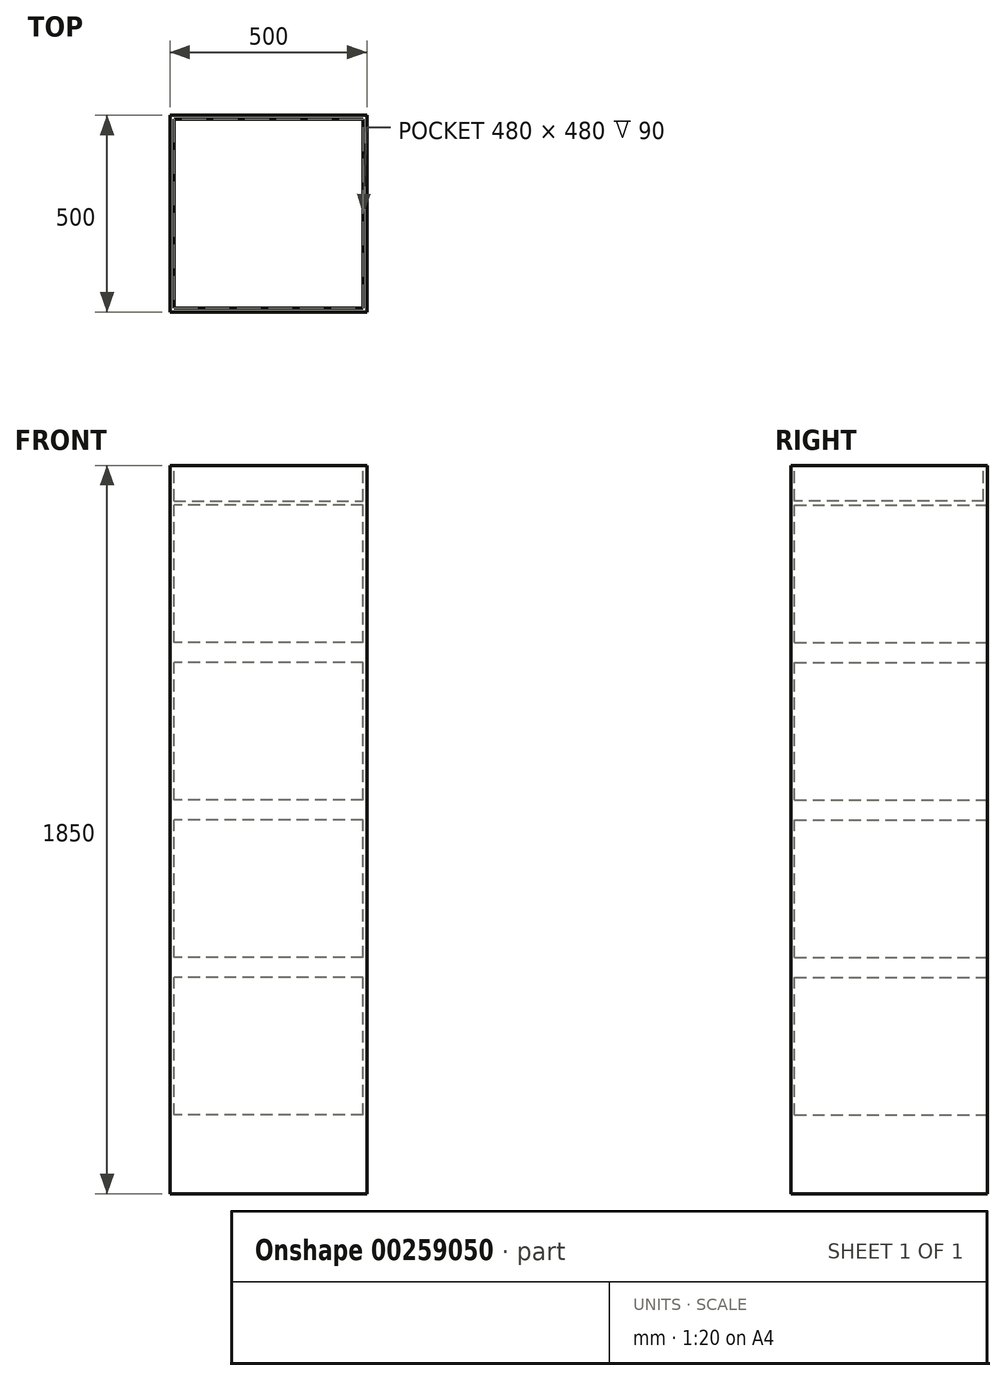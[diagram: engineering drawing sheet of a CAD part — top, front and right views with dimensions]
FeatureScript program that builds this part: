
annotation { "Feature Type Name" : "Feature", "Feature Type Description" : "" }
export const myFeature = defineFeature(function(context is Context, id is Id, definition is map)
    precondition{}
    {
        {
            var Q0;
            Q0=qCreatedBy(makeId("Top.planeOp"),FACE);
            var sketch = newSketch(context, id + "F0", { "sketchPlane" : qUnion([Q0])});
            skLineSegment(sketch, "E0.bottom", {"start": v(0, 0) * mm, "end": v(-500, 0) * mm});
            skLineSegment(sketch, "E0.top", {"start": v(0, 500) * mm, "end": v(-500, 500) * mm});
            skLineSegment(sketch, "E0.left", {"start": v(0, 0) * mm, "end": v(0, 500) * mm});
            skLineSegment(sketch, "E0.right", {"start": v(-500, 0) * mm, "end": v(-500, 500) * mm});
            skSolve(sketch);
        }
        {
            var Q0;
            Q0=makeQuery(id+"F0.imprint","IMPRINT",FACE,{"disambiguationData":[TD([[makeQuery(id+"F0.imprint","IMPRINT",EDGE,{"derivedFrom":sQuery(id+"F0.wireOp",EDGE,"E0.bottom")}),-1.0]])]});
            extrude(context, id + "F1", {"entities" : qUnion([Q0]), "depth" : 1850 * mm});
        }
        {
            var Q0;
            Q0=makeQuery(id+"F1.opExtrude","SWEPT_FACE",FACE,{"disambiguationData":[OSD([sQuery(id+"F0.wireOp",EDGE,"E0.top")])]});
            var sketch = newSketch(context, id + "F2", { "sketchPlane" : qUnion([Q0])});
            skLineSegment(sketch, "E1.bottom", {"start": v(10, 200) * mm, "end": v(490, 200) * mm});
            skLineSegment(sketch, "E1.top", {"start": v(10, 550) * mm, "end": v(490, 550) * mm});
            skLineSegment(sketch, "E1.left", {"start": v(10, 200) * mm, "end": v(10, 550) * mm});
            skLineSegment(sketch, "E1.right", {"start": v(490, 200) * mm, "end": v(490, 550) * mm});
            skLineSegment(sketch, "E2.bottom", {"start": v(10, 600) * mm, "end": v(490, 600) * mm});
            skLineSegment(sketch, "E2.top", {"start": v(10, 950) * mm, "end": v(490, 950) * mm});
            skLineSegment(sketch, "E2.left", {"start": v(10, 600) * mm, "end": v(10, 950) * mm});
            skLineSegment(sketch, "E2.right", {"start": v(490, 600) * mm, "end": v(490, 950) * mm});
            skLineSegment(sketch, "E3.bottom", {"start": v(10, 1000) * mm, "end": v(490, 1000) * mm});
            skLineSegment(sketch, "E3.top", {"start": v(10, 1350) * mm, "end": v(490, 1350) * mm});
            skLineSegment(sketch, "E3.left", {"start": v(10, 1000) * mm, "end": v(10, 1350) * mm});
            skLineSegment(sketch, "E3.right", {"start": v(490, 1000) * mm, "end": v(490, 1350) * mm});
            skLineSegment(sketch, "E4.bottom", {"start": v(10, 1400) * mm, "end": v(490, 1400) * mm});
            skLineSegment(sketch, "E4.top", {"start": v(10, 1750) * mm, "end": v(490, 1750) * mm});
            skLineSegment(sketch, "E4.left", {"start": v(10, 1400) * mm, "end": v(10, 1750) * mm});
            skLineSegment(sketch, "E4.right", {"start": v(490, 1400) * mm, "end": v(490, 1750) * mm});
            skSolve(sketch);
        }
        {
            var Q0;
            Q0=makeQuery(id+"F2.imprint","IMPRINT",FACE,{"disambiguationData":[TD([[makeQuery(id+"F2.imprint","IMPRINT",EDGE,{"derivedFrom":sQuery(id+"F2.wireOp",EDGE,"E4.bottom")}),1.0]])]});
            var Q1;
            Q1=makeQuery(id+"F2.imprint","IMPRINT",FACE,{"disambiguationData":[TD([[makeQuery(id+"F2.imprint","IMPRINT",EDGE,{"derivedFrom":sQuery(id+"F2.wireOp",EDGE,"E3.bottom")}),1.0]])]});
            var Q2;
            Q2=makeQuery(id+"F2.imprint","IMPRINT",FACE,{"disambiguationData":[TD([[makeQuery(id+"F2.imprint","IMPRINT",EDGE,{"derivedFrom":sQuery(id+"F2.wireOp",EDGE,"E2.bottom")}),1.0]])]});
            var Q3;
            Q3=makeQuery(id+"F2.imprint","IMPRINT",FACE,{"disambiguationData":[TD([[makeQuery(id+"F2.imprint","IMPRINT",EDGE,{"derivedFrom":sQuery(id+"F2.wireOp",EDGE,"E1.bottom")}),1.0]])]});
            extrude(context, id + "F3", {"entities" : qUnion([Q0, Q1, Q2, Q3]), "operationType" : NewBodyOperationType.REMOVE, "oppositeDirection" : true, "depth" : 490 * mm});
        }
        {
            var Q0;
            Q0=makeQuery(id+"F1.opExtrude","CAP_FACE",FACE,{"disambiguationData":[OSD([sQuery(id+"F0.wireOp",EDGE,"E0.bottom"),sQuery(id+"F0.wireOp",EDGE,"E0.top"),sQuery(id+"F0.wireOp",EDGE,"E0.left"),sQuery(id+"F0.wireOp",EDGE,"E0.right")])],"isStart":false});
            var sketch = newSketch(context, id + "F4", { "sketchPlane" : qUnion([Q0])});
            skLineSegment(sketch, "E5.0.0", {"start": v(0, 0) * mm, "end": v(0, 500) * mm});
            skLineSegment(sketch, "E5.0.1", {"start": v(0, 500) * mm, "end": v(-500, 500) * mm});
            skLineSegment(sketch, "E5.0.2", {"start": v(-500, 500) * mm, "end": v(-500, 0) * mm});
            skLineSegment(sketch, "E5.0.3", {"start": v(-500, 0) * mm, "end": v(0, 0) * mm});
            skLineSegment(sketch, "E6.bottom", {"start": v(-490, 490) * mm, "end": v(-10, 490) * mm});
            skLineSegment(sketch, "E6.top", {"start": v(-490, 10) * mm, "end": v(-10, 10) * mm});
            skLineSegment(sketch, "E6.left", {"start": v(-490, 490) * mm, "end": v(-490, 10) * mm});
            skLineSegment(sketch, "E6.right", {"start": v(-10, 490) * mm, "end": v(-10, 10) * mm});
            skSolve(sketch);
        }
        {
            var Q0;
            Q0=makeQuery(id+"F4.imprint","IMPRINT",FACE,{"disambiguationData":[TD([[makeQuery(id+"F4.imprint","IMPRINT",EDGE,{"derivedFrom":sQuery(id+"F4.wireOp",EDGE,"E6.bottom")}),-1.0]])]});
            extrude(context, id + "F5", {"entities" : qUnion([Q0]), "operationType" : NewBodyOperationType.REMOVE, "oppositeDirection" : true, "depth" : 90 * mm});
        }
    });
